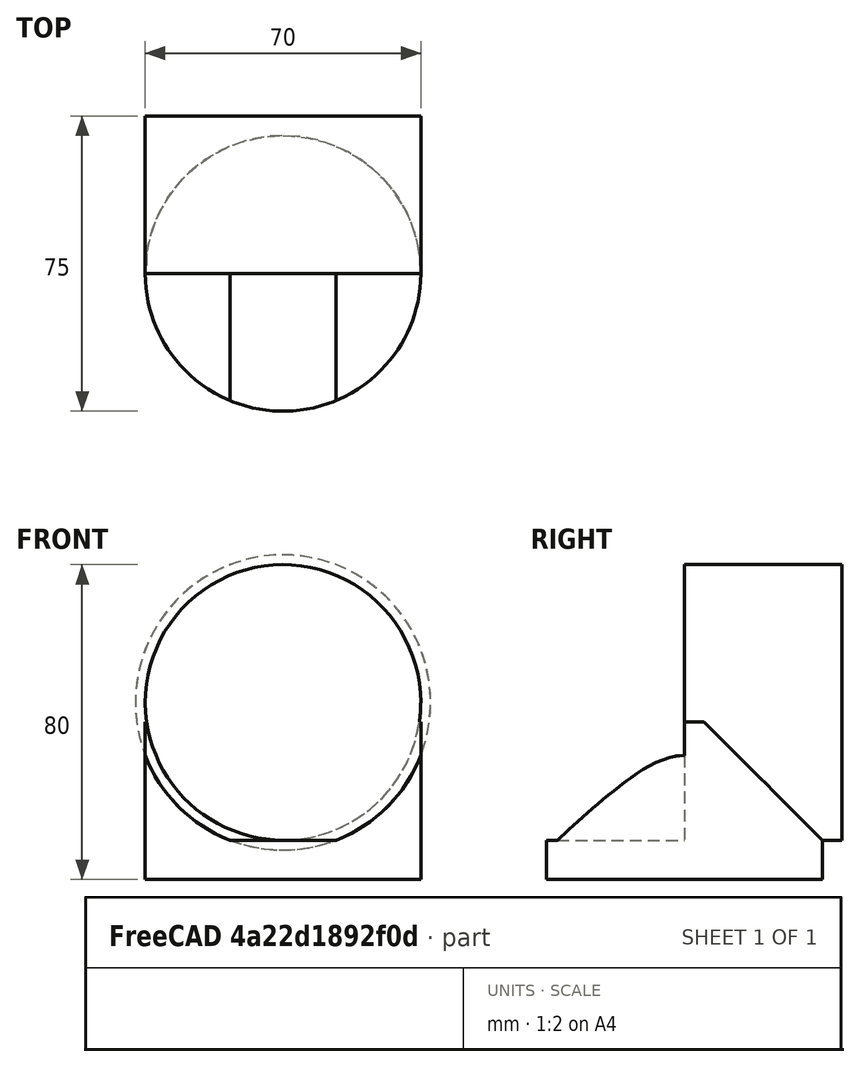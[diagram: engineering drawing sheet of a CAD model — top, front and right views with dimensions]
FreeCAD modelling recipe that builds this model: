
FCSTD DOCUMENT  (FreeCAD 0.19R24366 (Git))
Label: link_4
License: All rights reserved
LicenseURL: http://en.wikipedia.org/wiki/All_rights_reserved
objects: Sketcher::SketchObject×3, PartDesign::Pad×3, PartDesign::Pocket×1, PartDesign::Point×1, PartDesign::Body×1, Mesh::Feature×1
note: 13 computed .brp shape members not serialized (recipe doc carries the construction recipe); baked Part::Feature solids carry a one-line shape summary decoded from their .brp

FEATURE [Sketcher::SketchObject] Sketch
  FullyConstrained = true
  MapMode = 5
  Support = -> [XY_Plane]
  sketch-geometry (1):
    g0: Circle CenterX=0 CenterY=0 CenterZ=0 NormalX=0 NormalY=0 NormalZ=1 AngleXU=0 Radius=35
  constraints (2):
    c: Coincident(g0,g-1)
    c: Diameter(g0) = 70
FEATURE [PartDesign::Pad] Pad
  AllowMultiFace = false
  Direction = (1,1,1)
  Length = 30
  Length2 = 100
  Profile = -> Sketch
  Type = 0
FEATURE [Sketcher::SketchObject] Sketch001
  FullyConstrained = true
  MapMode = 5
  Placement = pos=(0,0,0) rot=(0.57735,0.57735,0.57735;2.0944rad)
  Support = -> [YZ_Plane]
  sketch-geometry (1):
    g0: Circle CenterX=0 CenterY=35 CenterZ=0 NormalX=0 NormalY=0 NormalZ=1 AngleXU=0 Radius=35
  constraints (3):
    c: PointOnObject(g0,g-2)
    c: Diameter(g0) = 70
    c: PointOnObject(g-1,g0)
FEATURE [PartDesign::Pad] Pad001
  BaseFeature = -> Pad
  Direction = (1,1,1)
  Length = 40
  Length2 = 100
  Profile = -> Sketch001
  Reversed = true
  Type = 0
FEATURE [Sketcher::SketchObject] Sketch002
  ExternalGeometry = -> [Sketch001]
  FullyConstrained = true
  MapMode = 5
  Placement = pos=(0,0,0) rot=(0.57735,0.57735,0.57735;2.0944rad)
  Support = -> [YZ_Plane]
  sketch-geometry (1):
    g0: Circle CenterX=0 CenterY=35 CenterZ=0 NormalX=0 NormalY=0 NormalZ=1 AngleXU=0 Radius=37.5
  constraints (2):
    c: Coincident(g-3,g0)
    c: Diameter(g0) = 75
FEATURE [PartDesign::Pocket] Pocket
  BaseFeature = -> Pad001
  Length = 35
  Length2 = 100
  Profile = -> Sketch002
  Reversed = true
  Type = 0
FEATURE [PartDesign::Pad] Pad002
  BaseFeature = -> Pocket
  Direction = (1,1,1)
  Length = 10
  Length2 = 100
  Profile = -> Sketch
  Reversed = true
  Type = 0
FEATURE [PartDesign::Point] DatumPoint
  AttacherType = Attacher::AttachEnginePoint
  MapMode = 36
  Placement = pos=(-40,7.1e-15,35) rot=(0.707107,0.707107,0;3.14159rad)
  Support = -> [Pad002]
FEATURE [PartDesign::Body] Body
  Group = -> [Sketch,Pad,Sketch001,Pad001,Sketch002,Pocket,Pad002,DatumPoint]
  Origin = -> Origin
  Placement = pos=(0,0,10) rot=(0,0,-1;1.5708rad)
  Tip = -> Pad002
FEATURE [Mesh::Feature] Mesh  label="Body (Meshed)"
